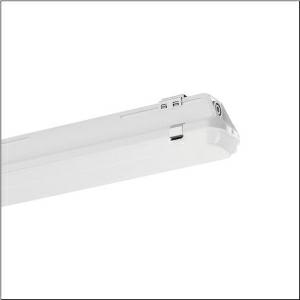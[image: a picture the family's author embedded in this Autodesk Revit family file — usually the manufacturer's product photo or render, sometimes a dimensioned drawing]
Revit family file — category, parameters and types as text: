
# Revit family: monsun_11_51fp10mp480h
name_source: partatom
category: Lighting Fixtures
units: mm (PartAtom-declared; Revit-internal decimal feet)

## family parameters
Cut with Voids When Loaded = No
Host = Face
Light Source = No
Part Type = Normal
Room Calculation Point = No
Round Connector Dimension = Use Diameter
Shared = No

## types (1)
- --- (1 x LED, 8070 lm, 45.4 W, 4000K)
    Apparent Load = 45 VA
    CIE Flux Codes = 47 77 93 94 100
    Color Rendering = 80
    Color Temperature = 4000K
    Default Elevation = 1800 mm
    Description = Monsun 11, damp-proof luminaire, chain hanger, primary optical cover: enclosure, of PMMA, light emission: direct distribution, primary light characteristic: symmetric, installation type: suspended mounting, surface-mounted, horizontal mounting, vertical mounting, LED, rated luminous flux: 8.070lm, luminous efficacy: 178lm/W, light colour: 840, colour temperature: 4000K, control gear: ON/OFF Multilumen, with terminal, 3-pole, max. 2.5mm², mains connection: 220..240V, AC, 50/60Hz, rated input power: 45W, luminaire housing, of glass-fibre reinforced polyester, uncoated, bright grey, incl. chain hanger, length: 1.590mm, width: 90mm, height: 88mm, clip for enclosure, of stainless steel (V2A), ceiling mounting element, of stainless steel (V2A), chain hanger, of stainless steel (V2A), protection rating (complete): IP66, insulation class (complete): insulation class I (protective earthing), certification: CE, ENEC, VDE, UKCA, protection symbol: D, impact resistance: IK04, permissible operating ambient temperature: -35..+40°C, standard: EN 50419, EN 60598-2-1, no direct snow, no direct sun, no direct rain, for indoor or canopied outdoor use, corresponds to IFS (International Featured Standards) requirements for safety and quality in the food industry, contact your sales advisor before using the luminaires in applications with unclear chemical exposure, large temperature fluctuations or condensation-forming humidity, LABS conformity tested according to VDMA 24364:2018-05, packaging unit: 1 piece
    Height = 89 mm
    Lamp = 1 x LED
    Lamp Light Flux = 8070 lm
    Lamp Power = 45.4 W
    Lamp count = 1
    Length = 1590 mm
    Luminous efficacy = 178 lm/W
    Manufacturer = Siteco
    ModVariant = No
    Model = 51FP10MP480H
    Mounting Place = Ceiling
    Mounting Type = Surface mounted
    Number of Poles = 1
    OnlyDefault = Yes
    Power Factor = 1
    Product Name = Monsun 11
    Product group = damp-proof luminaire
    ProductGroupID = 300
    Protection Class = Protection class I
    Protection Degree = IP 66
    RLX_Detail_Level = 1
    RLX_Emergency_Light_Flux = 0 lm
    RLX_Emergency_Type = 0
    RLX_Emergency_Type_DB = No
    RlxData = <blob elided: 90005 chars, md5=cdb7e9bf>
    Socket = socket
    Standby Power = 0 W
    System Light Flux = 8070 lm
    System Power = 45 W
    Type Comments = factory setting: luminous flux: 100 % | (A | C | E) | 105 mA
    Type Image = l_1349237.jpg
    URL = http://relux.com
    VarID = @adj_195943
    Voltage = 0 V
    Weight = 0.00 kg
    Width = 90 mm

## geometry (parser evidence)
native form markers: Blend x4, Sweep x14
no freeform markers — native parametric forms only
